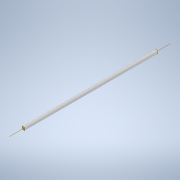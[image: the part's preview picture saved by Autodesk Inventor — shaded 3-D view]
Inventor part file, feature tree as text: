
AUTODESK INVENTOR PART (.ipt)
format: ipt  version: 2020 (Build 240168000, 168)  size: 164,864 bytes
history: native  units: in
note: dims shown in document units (in); Inventor stores cm internally (conversion verified against a paired STEP export)
features: other x5, extrude x1, imported_body x1, sketch x1
ambient origin geometry x8: Origin, YZ Plane, XZ Plane, XY Plane, X Axis, Y Axis, Z Axis, Center Point
bodies: Body1 (feature_tree)
feature tree (8):
  other  "Shaft HS 12.0 inch"
  other  "Cut-Revolve3"
  extrude  "Extrusion1"  TaperAngle=0.0deg  [1 undecoded]
  other  "Front Plane"
  other  "Work Axis1"
  imported_body  "Base1"
  other  "back plane"
  sketch  "Sketch1"  dims[d0=0.0in d2=0.0in d3=-12.0in d4=0.0in d5=0.0in d6=0.0in]
note: 1 required parameter value undecoded (feature->parameter linkage not recoverable at this tier; creation-order binding heuristic only, values carry confidence <= 0.55)
